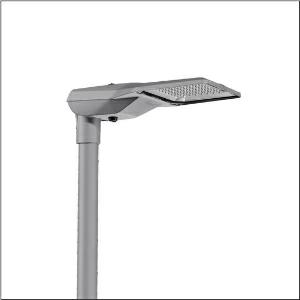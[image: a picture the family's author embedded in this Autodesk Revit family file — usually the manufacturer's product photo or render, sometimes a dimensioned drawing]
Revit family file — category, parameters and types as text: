
# Revit family: streetlight_sl_21_iq_midi___st1_0a_5xe3d41y08mb_a031
name_source: partatom
category: Lighting Fixtures
units: mm (PartAtom-declared; Revit-internal decimal feet)

## family parameters
Cut with Voids When Loaded = No
Host = Face
Light Source = No
Part Type = Normal
Room Calculation Point = No
Round Connector Dimension = Use Diameter
Shared = No

## types (1)
- --- (1 x LED, 18980 lm, 129.3 W, 4000K)
    Apparent Load = 129 VA
    CIE Flux Codes = 37 72 97 100 100
    Color Rendering = 70
    Color Temperature = 4000K
    Default Elevation = 1800 mm
    Description = Streetlight SL 21 iQ midi, mast luminaire, primary light control with lens, of PMMA, primary optical cover: cover, of toughened safety glass, transparent, light distribution: ST1.0a, light emission: direct distribution, primary light characteristic: asymmetric, installation type: post-top, side-entry, LED, High Power LED, rated luminous flux: 18.980lm, luminous efficacy: 147lm/W, light colour: 740, colour temperature: 4000K, control: presetting dimming logarithmic, Street-Remote, Auto-Match, Temp-Guard, Lumen-Switch, Night-Set, Smart-Wire, Light-Fading, Desk-Remote (wireless, voltage-free reading and setting of iQ features in the workshop via application-optimized NFC function/RFID function), optimised constant luminous flux control (CLO 2.0), mains connection: 230..240V, AC, 50/60Hz, start of lifetime: 129W, end of service life: 142W, reduction: 56W, luminaire housing, of diecast aluminium, powder-coated, Siteco® metallic grey (DB 702S), corrosivity category C5 mid according to DIN EN ISO 12944, please order mast flange separately, inclination adjustable: 0°, 5°, 10°, 15°, sealing non-destructively replaceable, multi-level sealing system, length: 644mm, width: 335mm, height: 110mm, mast flange for spigot size: 42mm (side-entry): 5XC10008XM4, 60/48mm (side-entry/post-top): 5XC10108XM2, 76/60mm (side-entry/post-top): 5XC10108XM1, Smart Interface below and above, protection rating (complete): IP66, insulation class (complete): insulation class II (safety insulation), certification: CE, ENEC, ENEC+, VDE, impact resistance: IK09, permissible operating ambient temperature for outdoor applications: -40..+50°C, standard-compliant lighting for roads and squares, packaging unit: 1 piece

Light Distribution: ST1.0a
    Height = 111 mm
    Lamp = 1 x LED
    Lamp Light Flux = 18980 lm
    Lamp Power = 129.3 W
    Lamp count = 1
    Length = 644 mm
    Luminous efficacy = 147 lm/W
    Manufacturer = Siteco
    ModVariant = No
    Model = 5XE3D41Y08MB
    Number of Poles = 1
    OnlyDefault = Yes
    Power Factor = 1
    Product Name = Streetlight SL 21 iQ midi | ST1.0a
    Product group = mast luminaire | pylon top
    ProductGroupID = 6100
    Protection Class = Protection class II
    Protection Degree = IP 66
    RLX_Detail_Level = 1
    RLX_Emergency_Light_Flux = 0 lm
    RLX_Emergency_Type = 0
    RLX_Emergency_Type_DB = No
    RlxData = <blob elided: 91125 chars, md5=9ece3d32>
    Socket = socket
    Standby Power = 0 W
    System Light Flux = 18980 lm
    System Power = 129 W
    Type Comments = factory setting: luminous flux: 100 % | dim-lin: 254 | 672 mA
    Type Image = l_1004304.jpg
    URL = http://relux.com
    VarID = @adj_044493
    Voltage = 0 V
    Weight = 0.00 kg
    Width = 336 mm

## geometry (parser evidence)
native form markers: Blend x4, Sweep x12
no freeform markers — native parametric forms only
